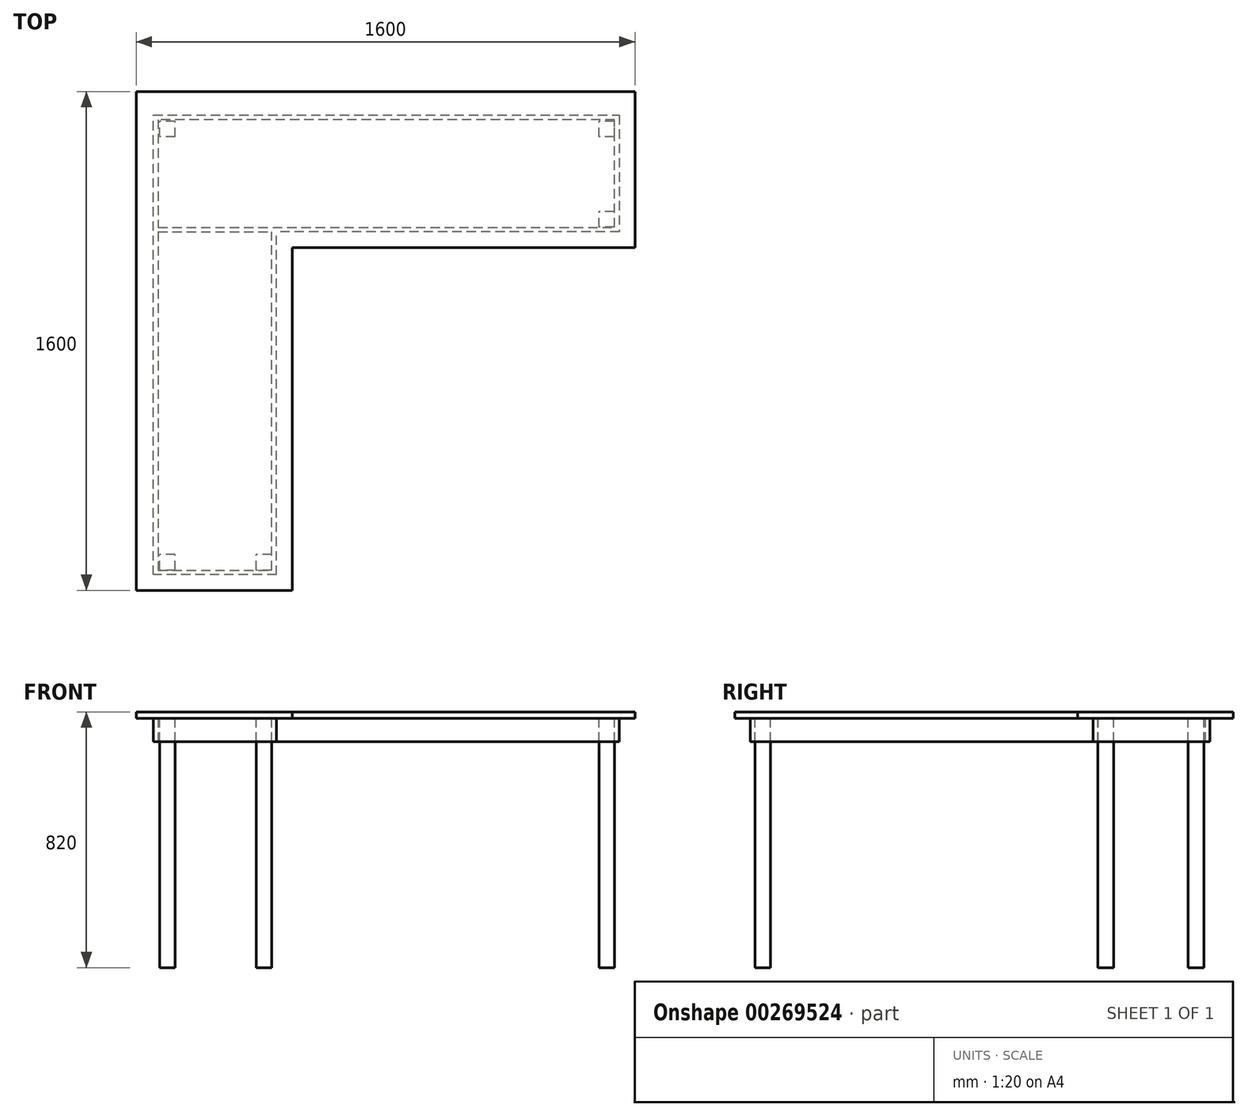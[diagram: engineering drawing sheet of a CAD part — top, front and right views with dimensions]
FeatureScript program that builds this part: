
annotation { "Feature Type Name" : "Feature", "Feature Type Description" : "" }
export const myFeature = defineFeature(function(context is Context, id is Id, definition is map)
    precondition{}
    {
        {
            var Q0;
            Q0=qCreatedBy(makeId("Top.planeOp"),FACE);
            var sketch = newSketch(context, id + "F0", { "sketchPlane" : qUnion([Q0])});
            skLineSegment(sketch, "E0.bottom", {"start": v(-777.96, 734.88) * mm, "end": v(-277.96, 734.88) * mm});
            skLineSegment(sketch, "E0.top", {"start": v(-777.96, -865.12) * mm, "end": v(-277.96, -865.12) * mm});
            skLineSegment(sketch, "E0.left", {"start": v(-777.96, 734.88) * mm, "end": v(-777.96, -865.12) * mm});
            skLineSegment(sketch, "E0.right", {"start": v(-277.96, 734.88) * mm, "end": v(-277.96, -865.12) * mm});
            skLineSegment(sketch, "E1.bottom", {"start": v(-277.96, 234.88) * mm, "end": v(822.04, 234.88) * mm});
            skLineSegment(sketch, "E1.top", {"start": v(-277.96, 734.88) * mm, "end": v(822.04, 734.88) * mm});
            skLineSegment(sketch, "E1.left", {"start": v(-277.96, 234.88) * mm, "end": v(-277.96, 734.88) * mm});
            skLineSegment(sketch, "E1.right", {"start": v(822.04, 234.88) * mm, "end": v(822.04, 734.88) * mm});
            skSolve(sketch);
        }
        {
            var Q0;
            Q0 = qSketchRegion(id + "F0", true);
            extrude(context, id + "F1", {"entities" : qUnion([Q0]), "depth" : 20 * mm});
        }
        {
            var Q0;
            Q0=qCreatedBy(makeId("Top.planeOp"),FACE);
            var sketch = newSketch(context, id + "F2", { "sketchPlane" : qUnion([Q0])});
            skLineSegment(sketch, "E2.bottom", {"start": v(-327.96, -815.12) * mm, "end": v(-342.96, -815.12) * mm});
            skLineSegment(sketch, "E2.top", {"start": v(-327.96, 284.88) * mm, "end": v(-342.96, 284.88) * mm});
            skLineSegment(sketch, "E2.left", {"start": v(-327.96, -815.12) * mm, "end": v(-327.96, 284.88) * mm});
            skLineSegment(sketch, "E2.right", {"start": v(-342.96, -815.12) * mm, "end": v(-342.96, 284.88) * mm});
            skSolve(sketch);
        }
        {
            var Q0;
            Q0=makeQuery(id+"F2.imprint","IMPRINT",FACE,{"disambiguationData":[TD([[makeQuery(id+"F2.imprint","IMPRINT",EDGE,{"derivedFrom":sQuery(id+"F2.wireOp",EDGE,"E2.bottom")}),-1.0]])]});
            extrude(context, id + "F3", {"entities" : qUnion([Q0]), "oppositeDirection" : true, "depth" : 75 * mm});
        }
        {
            var Q0;
            Q0=makeQuery(id+"F3.opExtrude","SWEPT_FACE",FACE,{"disambiguationData":[OSD([sQuery(id+"F2.wireOp",EDGE,"E2.right")])]});
            var sketch = newSketch(context, id + "F4", { "sketchPlane" : qUnion([Q0])});
            skLineSegment(sketch, "E3.bottom", {"start": v(815.12, 0) * mm, "end": v(800.12, 0) * mm});
            skLineSegment(sketch, "E3.top", {"start": v(815.12, -75) * mm, "end": v(800.12, -75) * mm});
            skLineSegment(sketch, "E3.left", {"start": v(815.12, 0) * mm, "end": v(815.12, -75) * mm});
            skLineSegment(sketch, "E3.right", {"start": v(800.12, 0) * mm, "end": v(800.12, -75) * mm});
            skSolve(sketch);
        }
        {
            var Q0;
            Q0=makeQuery(id+"F4.imprint","IMPRINT",FACE,{"disambiguationData":[TD([[makeQuery(id+"F4.imprint","IMPRINT",EDGE,{"derivedFrom":sQuery(id+"F4.wireOp",EDGE,"E3.bottom")}),1.0]])]});
            extrude(context, id + "F5", {"entities" : qUnion([Q0]), "operationType" : NewBodyOperationType.ADD, "depth" : 380 * mm});
        }
        {
            var Q0;
            Q0=makeQuery(id+"F5.opExtrude","SWEPT_FACE",FACE,{"disambiguationData":[OSD([sQuery(id+"F4.wireOp",EDGE,"E3.right")])]});
            var sketch = newSketch(context, id + "F6", { "sketchPlane" : qUnion([Q0])});
            skLineSegment(sketch, "E4.bottom", {"start": v(722.96, 0) * mm, "end": v(707.96, 0) * mm});
            skLineSegment(sketch, "E4.top", {"start": v(722.96, -75) * mm, "end": v(707.96, -75) * mm});
            skLineSegment(sketch, "E4.left", {"start": v(722.96, 0) * mm, "end": v(722.96, -75) * mm});
            skLineSegment(sketch, "E4.right", {"start": v(707.96, 0) * mm, "end": v(707.96, -75) * mm});
            skSolve(sketch);
        }
        {
            var Q0;
            Q0=makeQuery(id+"F6.imprint","IMPRINT",FACE,{"disambiguationData":[TD([[makeQuery(id+"F6.imprint","IMPRINT",EDGE,{"derivedFrom":sQuery(id+"F6.wireOp",EDGE,"E4.bottom")}),1.0]])]});
            extrude(context, id + "F7", {"entities" : qUnion([Q0]), "operationType" : NewBodyOperationType.ADD, "depth" : 1460 * mm});
        }
        {
            var Q0;
            Q0=makeQuery(id+"F7.opExtrude","SWEPT_FACE",FACE,{"disambiguationData":[OSD([sQuery(id+"F6.wireOp",EDGE,"E4.right")])]});
            var sketch = newSketch(context, id + "F8", { "sketchPlane" : qUnion([Q0])});
            skLineSegment(sketch, "E5.bottom", {"start": v(659.88, -75) * mm, "end": v(644.88, -75) * mm});
            skLineSegment(sketch, "E5.top", {"start": v(659.88, 0) * mm, "end": v(644.88, 0) * mm});
            skLineSegment(sketch, "E5.left", {"start": v(659.88, -75) * mm, "end": v(659.88, 0) * mm});
            skLineSegment(sketch, "E5.right", {"start": v(644.88, -75) * mm, "end": v(644.88, 0) * mm});
            skSolve(sketch);
        }
        {
            var Q0;
            Q0 = qSketchRegion(id + "F8", true);
            extrude(context, id + "F9", {"entities" : qUnion([Q0]), "depth" : 1480 * mm});
        }
        {
            var Q0;
            Q0=makeQuery(id+"F9.opExtrude","SWEPT_FACE",FACE,{"disambiguationData":[OSD([sQuery(id+"F8.wireOp",EDGE,"E5.right")])]});
            var sketch = newSketch(context, id + "F10", { "sketchPlane" : qUnion([Q0])});
            skLineSegment(sketch, "E6.bottom", {"start": v(772.04, -75) * mm, "end": v(757.04, -75) * mm});
            skLineSegment(sketch, "E6.top", {"start": v(772.04, 0) * mm, "end": v(757.04, 0) * mm});
            skLineSegment(sketch, "E6.left", {"start": v(772.04, -75) * mm, "end": v(772.04, 0) * mm});
            skLineSegment(sketch, "E6.right", {"start": v(757.04, -75) * mm, "end": v(757.04, 0) * mm});
            skSolve(sketch);
        }
        {
            var Q0;
            Q0 = qSketchRegion(id + "F10", true);
            extrude(context, id + "F11", {"entities" : qUnion([Q0]), "operationType" : NewBodyOperationType.ADD, "depth" : 360 * mm});
        }
        {
            var Q0;
            Q0=makeQuery(id+"F11.opExtrude","SWEPT_FACE",FACE,{"disambiguationData":[OSD([sQuery(id+"F10.wireOp",EDGE,"E6.right")])]});
            var sketch = newSketch(context, id + "F12", { "sketchPlane" : qUnion([Q0])});
            skLineSegment(sketch, "E7.bottom", {"start": v(-284.88, 0) * mm, "end": v(-299.88, 0) * mm});
            skLineSegment(sketch, "E7.top", {"start": v(-284.88, -75) * mm, "end": v(-299.88, -75) * mm});
            skLineSegment(sketch, "E7.left", {"start": v(-284.88, 0) * mm, "end": v(-284.88, -75) * mm});
            skLineSegment(sketch, "E7.right", {"start": v(-299.88, 0) * mm, "end": v(-299.88, -75) * mm});
            skSolve(sketch);
        }
        {
            var Q0;
            Q0=makeQuery(id+"F12.imprint","IMPRINT",FACE,{"disambiguationData":[TD([[makeQuery(id+"F12.imprint","IMPRINT",EDGE,{"derivedFrom":sQuery(id+"F12.wireOp",EDGE,"E7.bottom")}),1.0]])]});
            extrude(context, id + "F13", {"entities" : qUnion([Q0]), "operationType" : NewBodyOperationType.ADD, "endBound" : BoundingType.UP_TO_NEXT, "depth" : 1580 * mm});
        }
        {
            var Q0;
            Q0=makeQuery(id+"F1.opExtrude","CAP_FACE",FACE,{"disambiguationData":[OSD([sQuery(id+"F0.wireOp",EDGE,"E0.bottom"),sQuery(id+"F0.wireOp",EDGE,"E0.top"),sQuery(id+"F0.wireOp",EDGE,"E0.left"),sQuery(id+"F0.wireOp",EDGE,"E0.right"),sQuery(id+"F0.wireOp",EDGE,"E1.bottom"),sQuery(id+"F0.wireOp",EDGE,"E1.top"),sQuery(id+"F0.wireOp",EDGE,"E1.right")])],"isStart":true});
            var sketch = newSketch(context, id + "F14", { "sketchPlane" : qUnion([Q0])});
            skLineSegment(sketch, "E8.bottom", {"start": v(-342.96, 800.12) * mm, "end": v(-392.96, 800.12) * mm});
            skLineSegment(sketch, "E8.top", {"start": v(-342.96, 750.12) * mm, "end": v(-392.96, 750.12) * mm});
            skLineSegment(sketch, "E8.left", {"start": v(-342.96, 800.12) * mm, "end": v(-342.96, 750.12) * mm});
            skLineSegment(sketch, "E8.right", {"start": v(-392.96, 800.12) * mm, "end": v(-392.96, 750.12) * mm});
            skSolve(sketch);
        }
        {
            var Q0;
            {var subQ1=sQuery(id+"F14.wireOp",EDGE,"E8.top");Q0=makeQuery(id+"F14.imprint","IMPRINT",FACE,{"disambiguationData":[TD([[makeQuery(id+"F14.imprint","IMPRINT",EDGE,{"derivedFrom":subQ1}),-1.0]])]});}
            extrude(context, id + "F15", {"entities" : qUnion([Q0]), "depth" : 800 * mm});
        }
        {
            var Q0;
            Q0=makeQuery(id+"F15.opExtrude","SWEPT_BODY",BODY,{"disambiguationData":[OSD([sQuery(id+"F14.wireOp",EDGE,"E8.bottom"),sQuery(id+"F14.wireOp",EDGE,"E8.top"),sQuery(id+"F14.wireOp",EDGE,"E8.left"),sQuery(id+"F14.wireOp",EDGE,"E8.right")])]});
            transform(context, id + "F16", {"entities" : qUnion([Q0]), "transformType" : TransformType.TRANSLATION_3D, "dx" : -310 * mm, "dy" : 0 * mm, "dz" : 0 * mm, "makeCopy" : true});
        }
        {
            var Q0;
            Q0=makeQuery(id+"F16.opPattern","COPY",BODY,{"derivedFrom":makeQuery(id+"F15.opExtrude","SWEPT_BODY",BODY,{"disambiguationData":[OSD([sQuery(id+"F14.wireOp",EDGE,"E8.bottom"),sQuery(id+"F14.wireOp",EDGE,"E8.top"),sQuery(id+"F14.wireOp",EDGE,"E8.left"),sQuery(id+"F14.wireOp",EDGE,"E8.right")])]}),"instanceName":"1"});
            transform(context, id + "F17", {"entities" : qUnion([Q0]), "transformType" : TransformType.TRANSLATION_3D, "dx" : 0 * mm, "dy" : 1390 * mm, "dz" : 0 * mm, "makeCopy" : true});
        }
        {
            var Q0;
            Q0=makeQuery(id+"F17.opPattern","COPY",BODY,{"derivedFrom":makeQuery(id+"F16.opPattern","COPY",BODY,{"derivedFrom":makeQuery(id+"F15.opExtrude","SWEPT_BODY",BODY,{"disambiguationData":[OSD([sQuery(id+"F14.wireOp",EDGE,"E8.bottom"),sQuery(id+"F14.wireOp",EDGE,"E8.top"),sQuery(id+"F14.wireOp",EDGE,"E8.left"),sQuery(id+"F14.wireOp",EDGE,"E8.right")])]}),"instanceName":"1"}),"instanceName":"1"});
            transform(context, id + "F18", {"entities" : qUnion([Q0]), "transformType" : TransformType.TRANSLATION_3D, "dx" : 1409.5 * mm, "dy" : 0 * mm, "dz" : 0 * mm, "makeCopy" : true});
        }
        {
            var Q0;
            Q0=makeQuery(id+"F18.opPattern","COPY",BODY,{"derivedFrom":makeQuery(id+"F17.opPattern","COPY",BODY,{"derivedFrom":makeQuery(id+"F16.opPattern","COPY",BODY,{"derivedFrom":makeQuery(id+"F15.opExtrude","SWEPT_BODY",BODY,{"disambiguationData":[OSD([sQuery(id+"F14.wireOp",EDGE,"E8.bottom"),sQuery(id+"F14.wireOp",EDGE,"E8.top"),sQuery(id+"F14.wireOp",EDGE,"E8.left"),sQuery(id+"F14.wireOp",EDGE,"E8.right")])]}),"instanceName":"1"}),"instanceName":"1"}),"instanceName":"1"});
            transform(context, id + "F19", {"entities" : qUnion([Q0]), "transformType" : TransformType.TRANSLATION_3D, "dx" : 0 * mm, "dy" : -289.6 * mm, "dz" : 0 * mm, "makeCopy" : true});
        }
    });
